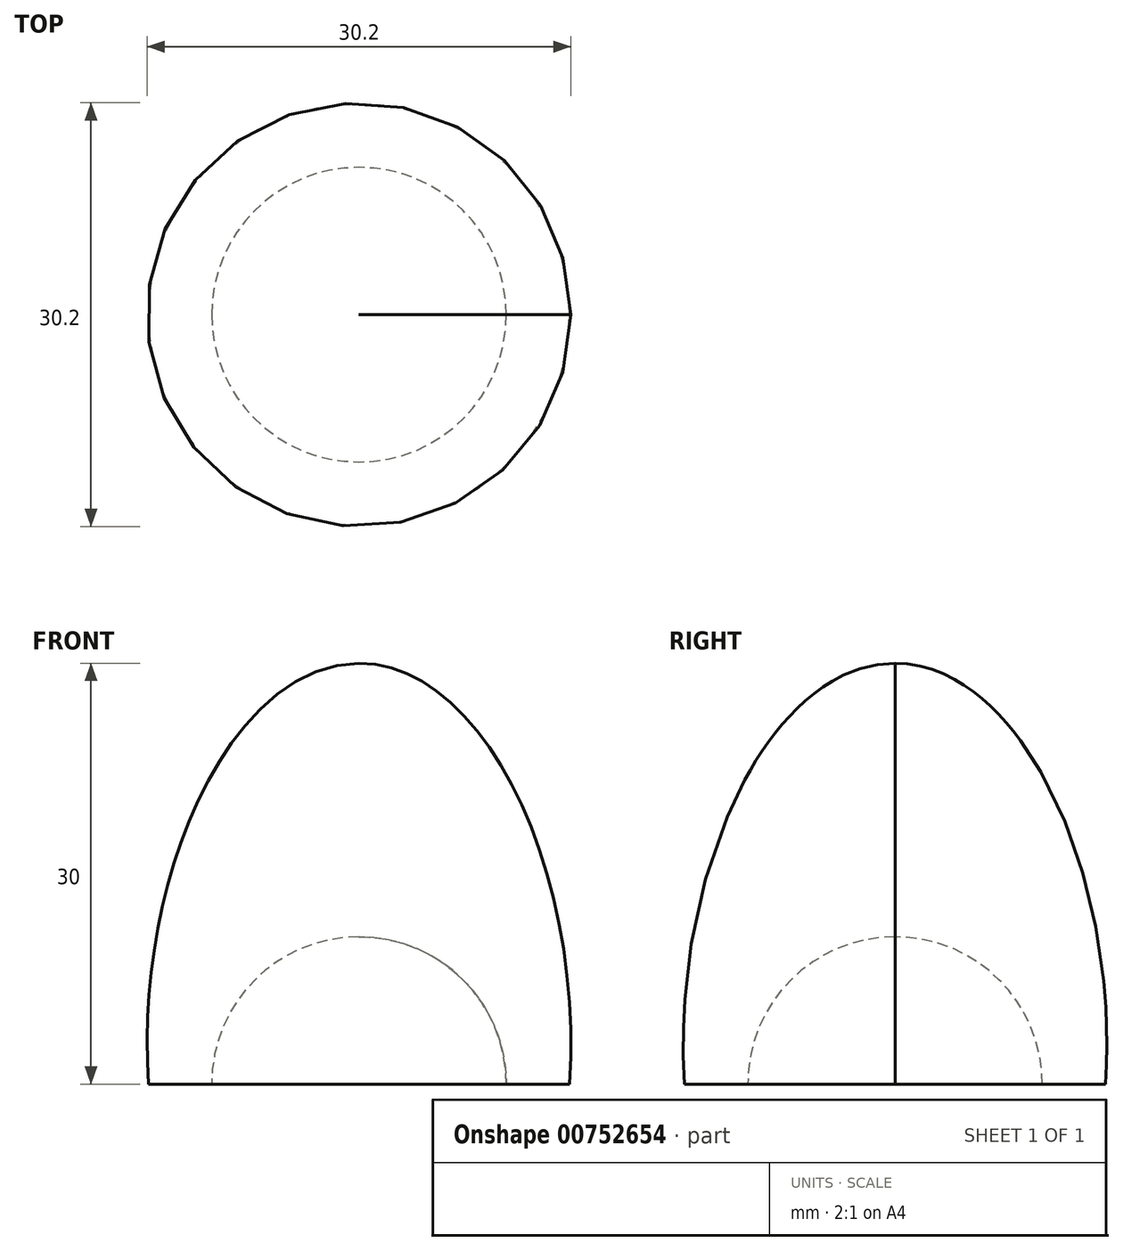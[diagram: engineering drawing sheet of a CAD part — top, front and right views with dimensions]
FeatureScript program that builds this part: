
annotation { "Feature Type Name" : "Feature", "Feature Type Description" : "" }
export const myFeature = defineFeature(function(context is Context, id is Id, definition is map)
    precondition{}
    {
        {
            var Q0;
            Q0=qCreatedBy(makeId("Front.planeOp"),FACE);
            var sketch = newSketch(context, id + "F0", { "sketchPlane" : qUnion([Q0])});
            skArc(sketch, "E0", {"start": v(10.5, 0) * mm, "mid": v(7.42, 7.42) * mm, "end": v(0, 10.5) * mm});
            skFitSpline(sketch, "E1", {"points": [v(0, 30) * mm, v(15, 0) * mm], "startDerivative": vector(27, 0) * mm, "endDerivative": vector(-3, -45) * mm});
            skLineSegment(sketch, "E2", {"start": v(0, 0) * mm, "end": v(0, 30) * mm});
            skLineSegment(sketch, "E3", {"start": v(0, 0) * mm, "end": v(15, 0) * mm});
            skSolve(sketch);
        }
        {
            var Q0;
            Q0=qCreatedBy(makeId("Top.planeOp"),FACE);
            var sketch = newSketch(context, id + "F1", { "sketchPlane" : qUnion([Q0])});
            skCircle(sketch, "E4", {"center": v(0, 0) * mm, "radius": 10 * mm, "construction": true});
            skSolve(sketch);
        }
        {
            var Q0;
            Q0=makeQuery(id+"F0.imprint","IMPRINT",FACE,{"disambiguationData":[TD([[makeQuery(id+"F0.imprint","IMPRINT",EDGE,{"derivedFrom":sQuery(id+"F0.wireOp",EDGE,"YeZH5L52-Gwtu-snDF-Z1ji-pw8hoUIH0mnF")}),-1.0]])]});
            var Q1;
            {var subQ0=sQuery(id+"F0.wireOp",EDGE,"E0");Q1=makeQuery(id+"F0.imprint","IMPRINT",FACE,{"disambiguationData":[TD([[makeQuery(id+"F0.imprint","IMPRINT",EDGE,{"derivedFrom":subQ0}),-1.0]])]});}
            var Q2;
            Q2=sQuery(id+"F1.wireOp",EDGE,"E4");
            revolve(context, id + "F2", {"entities" : qUnion([Q0, Q1]), "axis" : qUnion([Q2]), "revolveType" : RevolveType.FULL});
        }
    });
